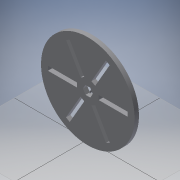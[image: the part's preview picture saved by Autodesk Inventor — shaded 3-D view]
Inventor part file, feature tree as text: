
AUTODESK INVENTOR PART (.ipt)
format: ipt  version: 2019 (Build 230136000, 136)  size: 157,184 bytes
history: native  units: mm
features: other x4, extrude x4, sketch x4, reference x4
ambient origin geometry x8: Origin, YZ Plane, XZ Plane, XY Plane, X Axis, Y Axis, Z Axis, Center Point
bodies: Body1 (feature_tree)
feature tree (16):
  other  "Твердое тело1"
  extrude  "Выдавливание1"  Depth=129.0mm
  extrude  "Выдавливание2"  Depth=6.0mm TaperAngle=0.0deg
  extrude  "Выдавливание3"  Depth=2.5mm
  extrude  "Выдавливание4"  Depth=6.0mm TaperAngle=0.0deg
  sketch  "Эскиз1"
  reference  "Ссылка1"
  sketch  "Эскиз2"
  reference  "Ссылка2"
  sketch  "Эскиз3"
  reference  "Ссылка3"
  sketch  "Эскиз4"
  reference  "Ссылка4"
  parser-record x1  (decoder bookkeeping rows leaked as tree rows — omitted from the tree; the rows remain in map.json)
  other  "kowsh.iam"
  other  "Двигатель:1"
note: 1 file-system path scrubbed to <path> (originals preserved in map.json)
